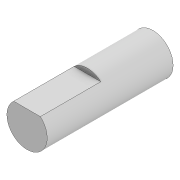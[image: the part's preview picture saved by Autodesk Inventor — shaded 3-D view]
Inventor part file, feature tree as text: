
AUTODESK INVENTOR PART (.ipt)
format: ipt  version: 2020 (Build 240168000, 168)  size: 84,480 bytes
history: native  units: mm
features: extrude x2, sketch x2, other x1
ambient origin geometry x8: Origin, YZ Plane, XZ Plane, XY Plane, X Axis, Y Axis, Z Axis, Center Point
bodies: Body1 (feature_tree)
feature tree (5):
  other  "솔리드1"
  extrude  "돌출1"  Depth=8.0mm
  extrude  "돌출2"  Depth=25.0mm TaperAngle=0.0deg
  sketch  "스케치1"
  sketch  "스케치2"
